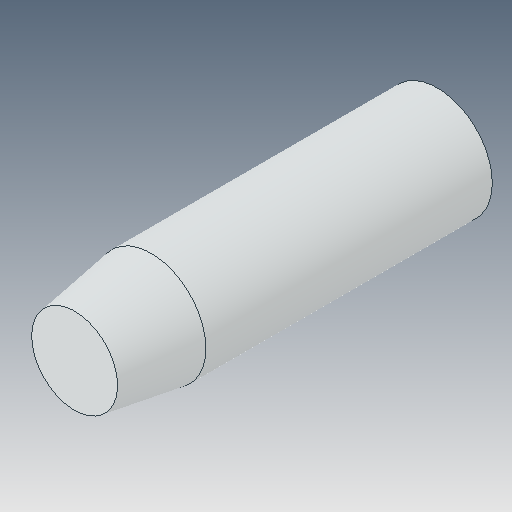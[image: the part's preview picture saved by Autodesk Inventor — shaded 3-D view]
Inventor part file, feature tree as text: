
AUTODESK INVENTOR PART (.ipt)
format: ipt  version: 2023.5 (Build 275446000, 446)  size: 98,304 bytes
history: native  units: in
note: dims shown in document units (in); Inventor stores cm internally (conversion verified against a paired STEP export)
features: chamfer x1
ambient origin geometry x8: Origin, YZ Plane, XZ Plane, XY Plane, X Axis, Y Axis, Z Axis, Center Point
bodies: Solid1 (feature_tree)
feature tree (1):
  chamfer  "Chamfer1"  [1 undecoded]
note: 1 required parameter value undecoded (feature->parameter linkage not recoverable at this tier; creation-order binding heuristic only, values carry confidence <= 0.55)
